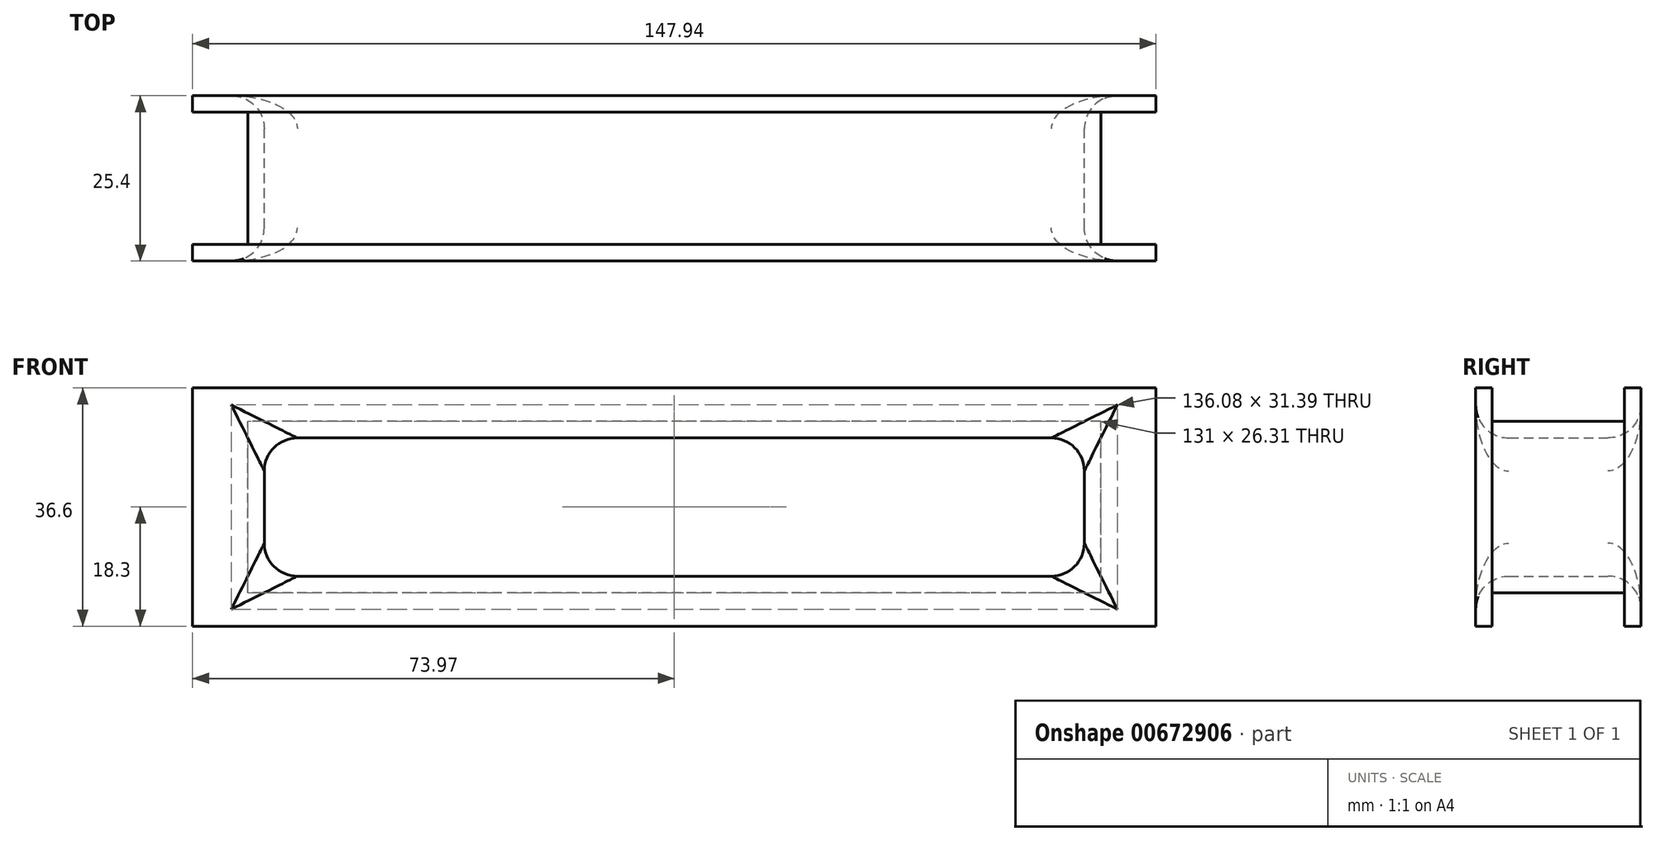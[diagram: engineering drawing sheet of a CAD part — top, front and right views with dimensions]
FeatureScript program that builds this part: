
annotation { "Feature Type Name" : "Feature", "Feature Type Description" : "" }
export const myFeature = defineFeature(function(context is Context, id is Id, definition is map)
    precondition{}
    {
        {
            var Q0;
            Q0=qCreatedBy(makeId("Front.planeOp"),FACE);
            var sketch = newSketch(context, id + "F0", { "sketchPlane" : qUnion([Q0])});
            skLineSegment(sketch, "E0.bottom", {"start": v(62.96, -10.62) * mm, "end": v(-62.96, -10.62) * mm});
            skLineSegment(sketch, "E0.top", {"start": v(62.96, 10.62) * mm, "end": v(-62.96, 10.62) * mm});
            skLineSegment(sketch, "E0.left", {"start": v(62.96, -10.62) * mm, "end": v(62.96, 10.62) * mm});
            skLineSegment(sketch, "E0.right", {"start": v(-62.96, -10.62) * mm, "end": v(-62.96, 10.62) * mm});
            skPoint(sketch, "E0.middle", {"position": v(0, 0) * mm});
            skLineSegment(sketch, "E1.bottom", {"start": v(73.97, 18.3) * mm, "end": v(-73.97, 18.3) * mm});
            skLineSegment(sketch, "E1.top", {"start": v(73.97, -18.3) * mm, "end": v(-73.97, -18.3) * mm});
            skLineSegment(sketch, "E1.left", {"start": v(73.97, 18.3) * mm, "end": v(73.97, -18.3) * mm});
            skLineSegment(sketch, "E1.right", {"start": v(-73.97, 18.3) * mm, "end": v(-73.97, -18.3) * mm});
            skSolve(sketch);
        }
        {
            var Q0;
            Q0 = qSketchRegion(id + "F0", true);
            extrude(context, id + "F1", {"entities" : qUnion([Q0]), "depth" : 25.4 * mm, "offsetDistance" : 25.4 * mm});
        }
        {
            var Q0;
            Q0=makeQuery(id+"F1.opExtrude","SWEPT_FACE",FACE,{"disambiguationData":[OSD([sQuery(id+"F0.wireOp",EDGE,"E1.bottom")])]});
            var Q1;
            Q1=makeQuery(id+"F1.opExtrude","SWEPT_FACE",FACE,{"disambiguationData":[OSD([sQuery(id+"F0.wireOp",EDGE,"E1.right")])]});
            var Q2;
            Q2=makeQuery(id+"F1.opExtrude","SWEPT_FACE",FACE,{"disambiguationData":[OSD([sQuery(id+"F0.wireOp",EDGE,"E1.top")])]});
            var Q3;
            Q3=makeQuery(id+"F1.opExtrude","SWEPT_FACE",FACE,{"disambiguationData":[OSD([sQuery(id+"F0.wireOp",EDGE,"E1.left")])]});
            shell(context, id + "F2", {"entities" : qUnion([Q0, Q1, Q2, Q3]), "thickness" : 2.54 * mm});
        }
        {
            var Q0;
            Q0=makeQuery(id+"F1.opExtrude","CAP_EDGE",EDGE,{"disambiguationData":[OSD([sQuery(id+"F0.wireOp",EDGE,"E0.top")])],"isStart":false});
            var Q1;
            Q1=makeQuery(id+"F1.opExtrude","CAP_EDGE",EDGE,{"disambiguationData":[OSD([sQuery(id+"F0.wireOp",EDGE,"E0.bottom")])],"isStart":false});
            var Q2;
            Q2=makeQuery(id+"F1.opExtrude","CAP_EDGE",EDGE,{"disambiguationData":[OSD([sQuery(id+"F0.wireOp",EDGE,"E0.left")])],"isStart":false});
            var Q3;
            Q3=makeQuery(id+"F1.opExtrude","CAP_EDGE",EDGE,{"disambiguationData":[OSD([sQuery(id+"F0.wireOp",EDGE,"E0.right")])],"isStart":false});
            var Q4;
            Q4=makeQuery(id+"F1.opExtrude","CAP_EDGE",EDGE,{"disambiguationData":[OSD([sQuery(id+"F0.wireOp",EDGE,"E0.right")])],"isStart":true});
            var Q5;
            Q5=makeQuery(id+"F1.opExtrude","CAP_EDGE",EDGE,{"disambiguationData":[OSD([sQuery(id+"F0.wireOp",EDGE,"E0.bottom")])],"isStart":true});
            var Q6;
            Q6=makeQuery(id+"F1.opExtrude","CAP_EDGE",EDGE,{"disambiguationData":[OSD([sQuery(id+"F0.wireOp",EDGE,"E0.left")])],"isStart":true});
            var Q7;
            Q7=makeQuery(id+"F1.opExtrude","CAP_EDGE",EDGE,{"disambiguationData":[OSD([sQuery(id+"F0.wireOp",EDGE,"E0.top")])],"isStart":true});
            fillet(context, id + "F3", {"entities" : qUnion([Q0, Q1, Q2, Q3, Q4, Q5, Q6, Q7]), "radius" : 5.08 * mm, "tangentPropagation" : true, "allowEdgeOverflow" : false});
        }
        {
            var Q0;
            Q0=makeQuery(id+"F1.opExtrude","SWEPT_FACE",FACE,{"disambiguationData":[OSD([sQuery(id+"F0.wireOp",EDGE,"E0.left")])]});
            var Q1;
            Q1=makeQuery(id+"F1.opExtrude","SWEPT_FACE",FACE,{"disambiguationData":[OSD([sQuery(id+"F0.wireOp",EDGE,"E0.bottom")])]});
            var Q2;
            Q2=makeQuery(id+"F1.opExtrude","SWEPT_FACE",FACE,{"disambiguationData":[OSD([sQuery(id+"F0.wireOp",EDGE,"E0.top")])]});
            var Q3;
            Q3=makeQuery(id+"F1.opExtrude","SWEPT_FACE",FACE,{"disambiguationData":[OSD([sQuery(id+"F0.wireOp",EDGE,"E0.right")])]});
            fillet(context, id + "F4", {"entities" : qUnion([Q0, Q1, Q2, Q3]), "radius" : 5.08 * mm, "tangentPropagation" : true, "allowEdgeOverflow" : false});
        }
    });
